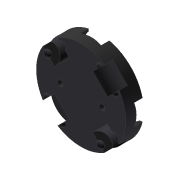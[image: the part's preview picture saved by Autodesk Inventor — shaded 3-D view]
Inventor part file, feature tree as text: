
AUTODESK INVENTOR PART (.ipt)
format: ipt  version: 2017 (Build 210142000, 142)  size: 213,504 bytes
history: native  units: mm
features: sketch x4, revolve x2, pattern_circular x2, extrude x1, hole x1, projected_geometry x1
ambient origin geometry x8: Origin, YZ Plane, XZ Plane, XY Plane, X Axis, Y Axis, Z Axis, Center Point
bodies: Solid1 (feature_tree)
feature tree (11):
  extrude  "Extrusion1"  Depth=18.0mm
  revolve  "Revolution1"  [1 undecoded]
  pattern_circular  "Circular Pattern1"  [2 undecoded]
  revolve  "Revolution2"  [1 undecoded]
  pattern_circular  "Circular Pattern2"  [2 undecoded]
  hole  "Hole1"  [1 undecoded]
  sketch  "Sketch1"  dims[d0=60.0mm d1=18.0mm]
  sketch  "Sketch2"  dims[d2=7.0mm d3=14.0mm]
  sketch  "Sketch3"  dims[d4=0.0mm]
  projected_geometry  "Projected Loop1"
  sketch  "Sketch4"  dims[d5=2.5mm d6=2.5mm d7=2.5mm d8=2.5mm d9=2.5mm d10=2.5mm d11=12.0mm d12=0.0mm d13=18.0mm d14=7.0mm d15=14.0mm d16=0.0mm d17=5.0mm d18=5.0mm d19=90.0deg d20=40.0mm d21=360.0deg d23=25.0mm d24=45.0deg d25=14.0mm d26=90.0deg d27=14.0mm d28=5.0mm d29=5.0mm d30=90.0deg d31=40.0mm d32=360.0deg d34=14.0mm d35=14.0mm d36=4.0mm d37=6.0mm d38=4.0mm d39=2.0mm d40=90.0deg d41=8.0mm d42=20.594885mm]
note: 7 required parameter values undecoded (feature->parameter linkage not recoverable at this tier; creation-order binding heuristic only, values carry confidence <= 0.55)